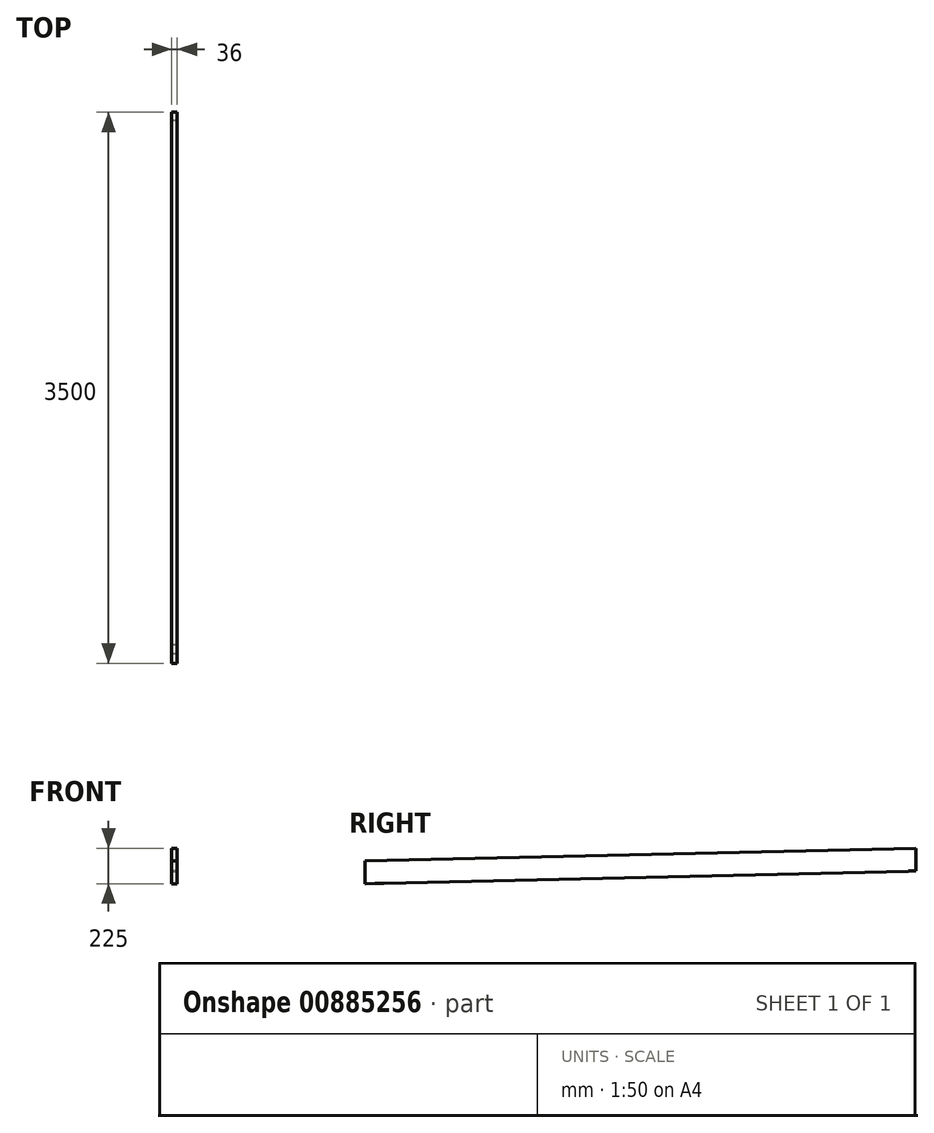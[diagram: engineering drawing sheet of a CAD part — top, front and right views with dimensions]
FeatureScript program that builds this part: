
annotation { "Feature Type Name" : "Feature", "Feature Type Description" : "" }
export const myFeature = defineFeature(function(context is Context, id is Id, definition is map)
    precondition{}
    {
        {
            var Q0;
            Q0=qCreatedBy(makeId("Right.planeOp"),FACE);
            var sketch = newSketch(context, id + "F0", { "sketchPlane" : qUnion([Q0])});
            skLineSegment(sketch, "E0", {"start": v(-1638.09, -145) * mm, "end": v(1861.91, -65) * mm});
            skLineSegment(sketch, "E1", {"start": v(1861.91, -65) * mm, "end": v(1861.91, 80) * mm});
            skLineSegment(sketch, "E2", {"start": v(1861.91, 80) * mm, "end": v(-1638.09, 0) * mm});
            skLineSegment(sketch, "E3", {"start": v(-1638.09, 0) * mm, "end": v(-1638.09, -145) * mm});
            skSolve(sketch);
        }
        {
            var Q0;
            Q0 = qSketchRegion(id + "F0", true);
            extrude(context, id + "F1", {"entities" : qUnion([Q0]), "depth" : 36 * mm, "offsetDistance" : 25 * mm});
        }
        {
            var Q0;
            Q0=makeQuery(id+"F1.opExtrude","CAP_FACE",FACE,{"disambiguationData":[OSD([sQuery(id+"F0.wireOp",EDGE,"E0"),sQuery(id+"F0.wireOp",EDGE,"E1"),sQuery(id+"F0.wireOp",EDGE,"E2"),sQuery(id+"F0.wireOp",EDGE,"E3")])],"isStart":false});
            var sketch = newSketch(context, id + "F2", { "sketchPlane" : qUnion([Q0])});
            skLineSegment(sketch, "E4", {"start": v(1861.91, -65) * mm, "end": v(1811.91, -65) * mm});
            skLineSegment(sketch, "E5", {"start": v(1811.91, -65) * mm, "end": v(1811.91, -79.73) * mm});
            skLineSegment(sketch, "E6", {"start": v(1811.91, -79.73) * mm, "end": v(1874.58, -79.73) * mm});
            skLineSegment(sketch, "E7", {"start": v(1874.58, -79.73) * mm, "end": v(1861.91, -65) * mm});
            skSolve(sketch);
        }
        {
            var Q0;
            Q0 = qSketchRegion(id + "F2", true);
            extrude(context, id + "F3", {"entities" : qUnion([Q0]), "operationType" : NewBodyOperationType.REMOVE, "endBound" : BoundingType.THROUGH_ALL, "oppositeDirection" : true, "depth" : 25 * mm, "offsetDistance" : 25 * mm});
        }
        {
            var Q0;
            Q0=makeQuery(id+"F1.opExtrude","CAP_FACE",FACE,{"disambiguationData":[OSD([sQuery(id+"F0.wireOp",EDGE,"E0"),sQuery(id+"F0.wireOp",EDGE,"E1"),sQuery(id+"F0.wireOp",EDGE,"E2"),sQuery(id+"F0.wireOp",EDGE,"E3")])],"isStart":false});
            var sketch = newSketch(context, id + "F4", { "sketchPlane" : qUnion([Q0])});
            skLineSegment(sketch, "E8", {"start": v(-1518.09, -142.26) * mm, "end": v(-1574.83, -142.26) * mm});
            skLineSegment(sketch, "E9", {"start": v(-1574.83, -142.26) * mm, "end": v(-1574.83, -160.75) * mm});
            skLineSegment(sketch, "E10", {"start": v(-1574.83, -160.75) * mm, "end": v(-1516.12, -160.75) * mm});
            skLineSegment(sketch, "E11", {"start": v(-1516.12, -160.75) * mm, "end": v(-1518.09, -142.26) * mm});
            skSolve(sketch);
        }
        {
            var Q0;
            Q0 = qSketchRegion(id + "F4", true);
            extrude(context, id + "F5", {"entities" : qUnion([Q0]), "operationType" : NewBodyOperationType.REMOVE, "endBound" : BoundingType.THROUGH_ALL, "oppositeDirection" : true, "depth" : 25 * mm, "offsetDistance" : 25 * mm});
        }
    });
